# Revit family: Furniture_Armchairs_LDK-Living-Outdoors_KARMAN-Lounge-Chair
name_source: partatom
category: Furniture
units: mm (PartAtom-declared; Revit-internal decimal feet)

## family parameters
Always vertical = No
Cut with Voids When Loaded = No
OmniClass Number = 23.11.29.13
OmniClass Title = Exterior Seating
Room Calculation Point = No
Shared = No
Work Plane-Based = Yes

## types (1)
- KARMAN Lounge Chair
    Assembly Code = E2020200
    Date Updated = 30/09/2024
    Default Elevation = 0 mm  [stored 0 ft]
    Depth = 830 mm  [stored 2.7231 ft]
    Description = The Kármán collection consists of 4 pieces (1 swivel seat, 2 seats and 3 seats). Complete aluminium structure. Hand-woven with olefin rope in beige or graphite; upholstery in dove-coloured Saint Tropez series olefin. UV, stain, mildew and water resistant. Easy to clean.
    Frame Material = LDK Outdoors - Rope - Beige
    Height = 720 mm  [stored 2.3622 ft]
    Keynote = 12000
    Manufacturer = LdK Living Outdoors
    Model = KARMAN Lounge Chair
    Product Page URL = https://b2b.ldkoutdoors.es
    Product data url = https://bimobject.com
    URL = https://b2b.ldkoutdoors.es
    Upholstery Material = LDK Outdoors - Fabric - St. Tropez Dove
    Version = 1
    Width = 860 mm

note: [stored X ft] marks values corroborated as IEEE doubles in the binary element streams (Revit-internal decimal feet)

## geometry (parser evidence)
native form markers: Sweep x3
no freeform markers — native parametric forms only
